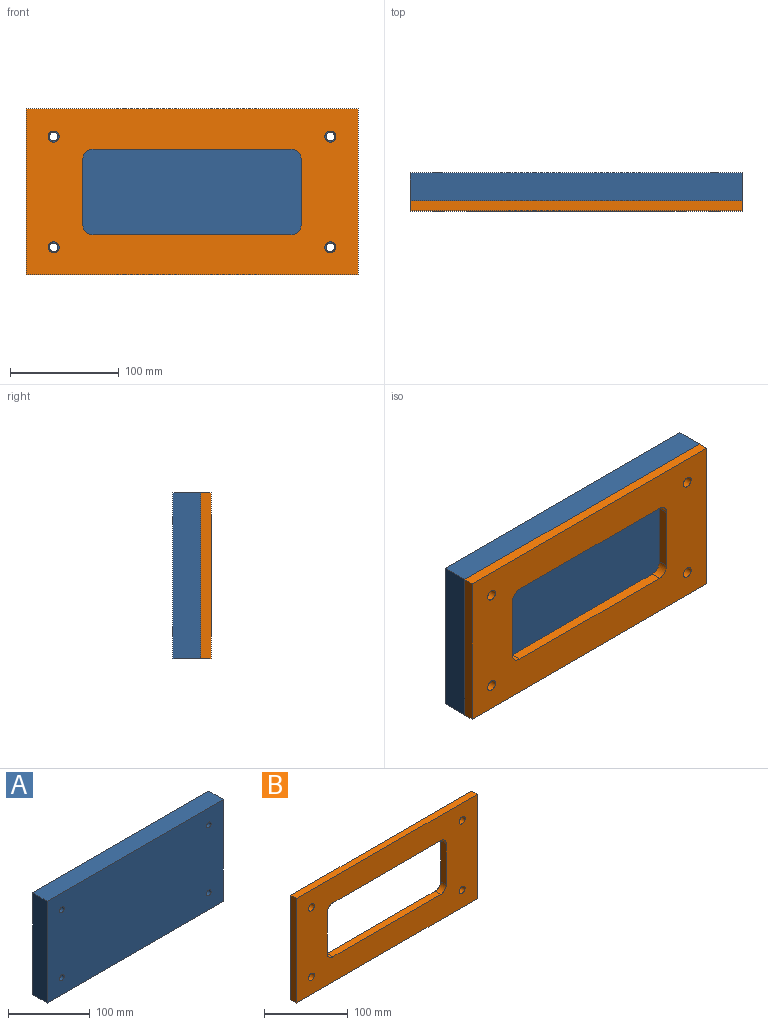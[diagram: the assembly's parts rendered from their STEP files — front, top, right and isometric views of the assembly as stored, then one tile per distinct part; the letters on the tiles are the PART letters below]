
ASSEMBLY  parts=2 mates=1
PART A: 10 faces, bbox 304.8x25.4x152.4 mm
  f0: plane 304.8x25.4mm, normal (0,0,-1), area 7741.9mm2, adj f1,f3,f4,f5
  f1: plane 152.4x25.4mm, normal (1,0,0), area 3871mm2, adj f0,f2,f4,f5
  f2: plane 304.8x25.4mm, normal (0,0,1), area 7741.9mm2, adj f1,f3,f4,f5
  f3: plane 152.4x25.4mm, normal (-1,0,0), area 3871mm2, adj f0,f2,f4,f5
  f4: plane 304.8x152.4mm, normal (0,-1,0), area 46253.6mm2, adj f0,f1,f2,f3,f6,f7,f8,f9
  f5: plane 304.8x152.4mm, normal (0,1,0), area 46253.6mm2, adj f0,f1,f2,f3,f6,f7,f8,f9
  f6: cylinder r=3.97mm len=25.4mm, axis (0,-1,0), area 633.4mm2, adj f4,f5
  f7: cylinder r=3.97mm len=25.4mm, axis (0,-1,0), area 633.4mm2, adj f4,f5
  f8: cylinder r=3.97mm len=25.4mm, axis (0,-1,0), area 633.4mm2, adj f4,f5
  f9: cylinder r=3.97mm len=25.4mm, axis (0,-1,0), area 633.4mm2, adj f4,f5
PART B: 18 faces, bbox 304.8x9.5x152.4 mm
  f0: plane 304.8x152.4mm, normal (0,-1,0), area 30410mm2, adj f2,f3,f4,f5,f6,f7,f8,f9
  f1: plane 304.8x152.4mm, normal (0,1,0), area 30410mm2, adj f2,f3,f4,f5,f6,f7,f8,f9
  f2: plane 304.8x9.53mm, normal (0,0,-1), area 2903.2mm2, adj f0,f1,f3,f5
  f3: plane 152.4x9.53mm, normal (1,0,0), area 1451.6mm2, adj f0,f1,f2,f4
  f4: plane 304.8x9.53mm, normal (0,0,1), area 2903.2mm2, adj f0,f1,f3,f5
  f5: plane 152.4x9.53mm, normal (-1,0,0), area 1451.6mm2, adj f0,f1,f2,f4
  f6: plane 181.61x9.53mm, normal (0,0,1), area 1729.8mm2, adj f0,f1,f10,f13
  f7: plane 59.69x9.53mm, normal (-1,0,0), area 568.5mm2, adj f0,f1,f10,f11
  f8: plane 181.61x9.53mm, normal (0,0,-1), area 1729.8mm2, adj f0,f1,f11,f12
  f9: plane 59.69x9.53mm, normal (1,0,0), area 568.5mm2, adj f0,f1,f12,f13
  f10: cylinder r=9.53mm len=9.53mm, axis (0,-1,0), area 142.5mm2, adj f0,f1,f6,f7
  f11: cylinder r=9.53mm len=9.53mm, axis (0,1,0), area 142.5mm2, adj f0,f1,f7,f8
  f12: cylinder r=9.53mm len=9.53mm, axis (0,-1,0), area 142.5mm2, adj f0,f1,f8,f9
  f13: cylinder r=9.53mm len=9.53mm, axis (0,1,0), area 142.5mm2, adj f0,f1,f6,f9
  f14: cylinder r=5.04mm len=10.08mm, axis (0,-1,0), area 301.7mm2, adj f0,f1
  f15: cylinder r=5.04mm len=10.08mm, axis (0,-1,0), area 301.7mm2, adj f0,f1
  f16: cylinder r=5.04mm len=10.08mm, axis (0,-1,0), area 301.7mm2, adj f0,f1
  f17: cylinder r=5.04mm len=10.08mm, axis (0,-1,0), area 301.7mm2, adj f0,f1
PLACE A at identity
PLACE B t=(0,-25.4,0)mm
MATE fastened B.f17 <-> A.f9  axis (0,1,0) through (127,-25.4,50.8)mm
